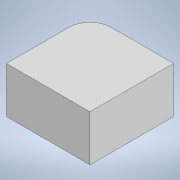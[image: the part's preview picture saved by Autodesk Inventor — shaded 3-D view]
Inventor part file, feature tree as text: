
AUTODESK INVENTOR PART (.ipt)
format: ipt  version: 2020 (Build 240168000, 168)  size: 90,624 bytes
history: native  units: mm
features: extrude x1, fillet x1, sketch x1
ambient origin geometry x8: Origin, YZ Plane, XZ Plane, XY Plane, X Axis, Y Axis, Z Axis, Center Point
bodies: Solide1 (feature_tree)
feature tree (3):
  extrude  "Extrusion1"  Depth=40.0mm
  fillet  "Congé1"  Radius=40.0mm
  sketch  "Esquisse1"
